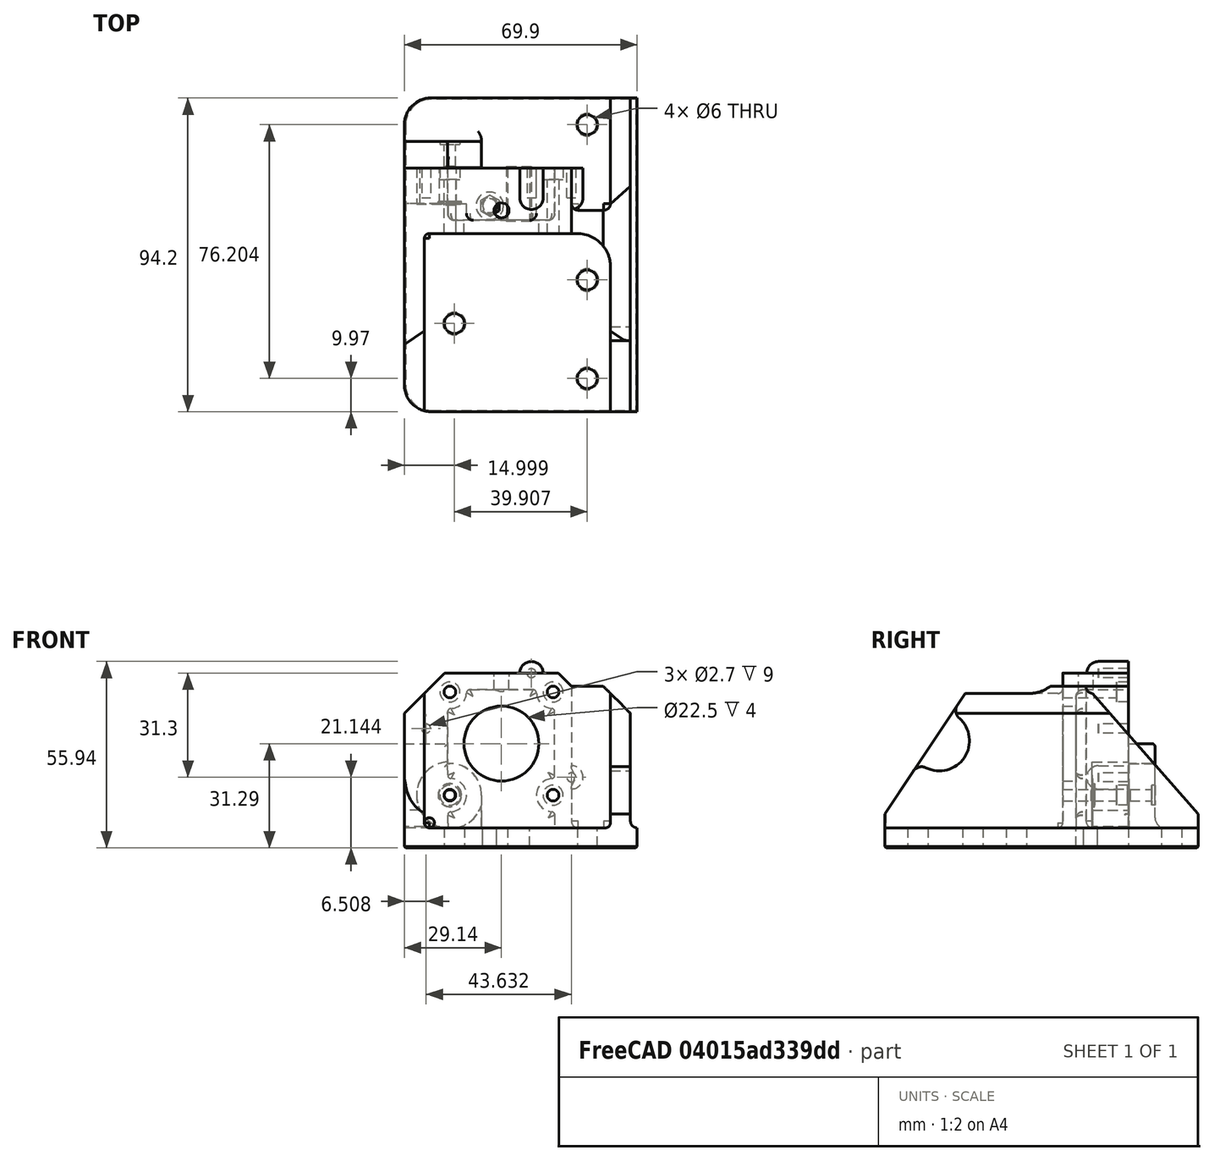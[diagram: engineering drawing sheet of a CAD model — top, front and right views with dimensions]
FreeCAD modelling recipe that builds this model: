
FCSTD DOCUMENT  (FreeCAD 0.18R16146 (Git))
Label: motor-mount-right-2
License: All rights reserved
LicenseURL: http://en.wikipedia.org/wiki/All_rights_reserved
objects: Part::Cylinder×7, Part::Cut×5, Part::Chamfer×5, Part::Feature×3, Part::MultiFuse×3
note: 23 computed .brp shape members not serialized (recipe doc carries the construction recipe); baked Part::Feature solids carry a one-line shape summary decoded from their .brp

FEATURE [Part::Feature] Part__Feature122  label="MotorBracket_RIGHT_Body V1.002"
  Placement = pos=(1.73891,-418.826,-435.206) rot=(0,1,0;3.14159rad)
  shape: bbox 69.9 x 94.2 x 55.94 mm, 170 faces (baked)
FEATURE [Part::Cylinder] Cylinder
  Angle = 360
  AttacherType = Attacher::AttachEngine3D
  Height = 0.75
  Placement = pos=(-56.26,72.325,15.8) rot=(-1,0,0;1.5708rad)
  Radius = 3.5
FEATURE [Part::Cylinder] Cylinder001
  Angle = 360
  AttacherType = Attacher::AttachEngine3D
  Height = 11
  Placement = pos=(-56.26,72.325,15.8) rot=(-1,0,0;1.5708rad)
  Radius = 10
FEATURE [Part::Cut] Cut
  Base = -> Part__Feature122
  Tool = -> Cylinder001
FEATURE [Part::Cylinder] Cylinder002
  Angle = 360
  AttacherType = Attacher::AttachEngine3D
  Height = 0.75
  Placement = pos=(-56.26,72.325,15.8) rot=(-1,0,0;1.5708rad)
  Radius = 1.65
FEATURE [Part::Chamfer] Chamfer
  Base = -> Cut
  Edges = 17 edges r=0.4: [Edge92,Edge101,Edge107,Edge155,Edge167,Edge170,Edge171,Edge188,Edge221,Edge222,Edge223,Edge224,Edge225,Edge226,Edge227,Edge228,Edge229]
FEATURE [Part::Cylinder] Cylinder003
  Angle = 360
  AttacherType = Attacher::AttachEngine3D
  Height = 10
  Placement = pos=(-40.77,61,31.29) rot=(-1,0,0;1.5708rad)
  Radius = 11.25
FEATURE [Part::Cut] Cut001003
  Base = -> Cylinder
  Tool = -> Cylinder002
FEATURE [Part::Feature] Cut001003001  label="Cut001004"
  Placement = pos=(0,-0.35,0) rot=(0,0,1;0rad)
  shape: bbox 7 x 0.75 x 7 mm, 4 faces (baked)
FEATURE [Part::Feature] Cut001003002  label="Cut001005"
  Placement = pos=(0,10.6,0) rot=(0,0,1;0rad)
  shape: bbox 7 x 0.75 x 7 mm, 4 faces (baked)
FEATURE [Part::Chamfer] Chamfer001
  Base = -> Cut001003001
  Edges = 1 edges r=0.5: [Edge1]
FEATURE [Part::Chamfer] Chamfer002
  Base = -> Cut001003002
  Edges = 1 edges r=0.5: [Edge3]
FEATURE [Part::MultiFuse] Fusion
  Shapes = -> [Chamfer002,Chamfer001]
FEATURE [Part::Cut] Cut001003003
  Base = -> Chamfer
  Tool = -> Cylinder003
FEATURE [Part::MultiFuse] Fusion001
  Shapes = -> [Cut001003003,Fusion]
FEATURE [Part::Cylinder] Cylinder004
  Angle = 360
  AttacherType = Attacher::AttachEngine3D
  Height = 6
  Placement = pos=(-44.27,71.84,0) rot=(0,0,1;0rad)
  Radius = 2.1
FEATURE [Part::Cylinder] Cylinder005
  Angle = 360
  AttacherType = Attacher::AttachEngine3D
  Height = 6
  Placement = pos=(-44.27,71.84,0) rot=(0,0,1;0rad)
  Radius = 2.1
FEATURE [Part::Cut] Cut001003004
  Base = -> Fusion001
  Tool = -> Cylinder004
FEATURE [Part::Cylinder] Cylinder006
  Angle = 360
  AttacherType = Attacher::AttachEngine3D
  Height = 6
  Placement = pos=(-44.27,71.84,0) rot=(0,0,1;0rad)
  Radius = 4.1
FEATURE [Part::Cut] Cut001003005
  Base = -> Cylinder006
  Tool = -> Cylinder005
FEATURE [Part::Chamfer] Chamfer003
  Base = -> Cut001003004
  Edges = 1 edges r=0.4: [Edge138]
FEATURE [Part::Chamfer] Chamfer004
  Base = -> Cut001003005
  Edges = 1 edges r=0.4: [Edge5]
FEATURE [Part::MultiFuse] Fusion002
  Shapes = -> [Chamfer004,Chamfer003]
